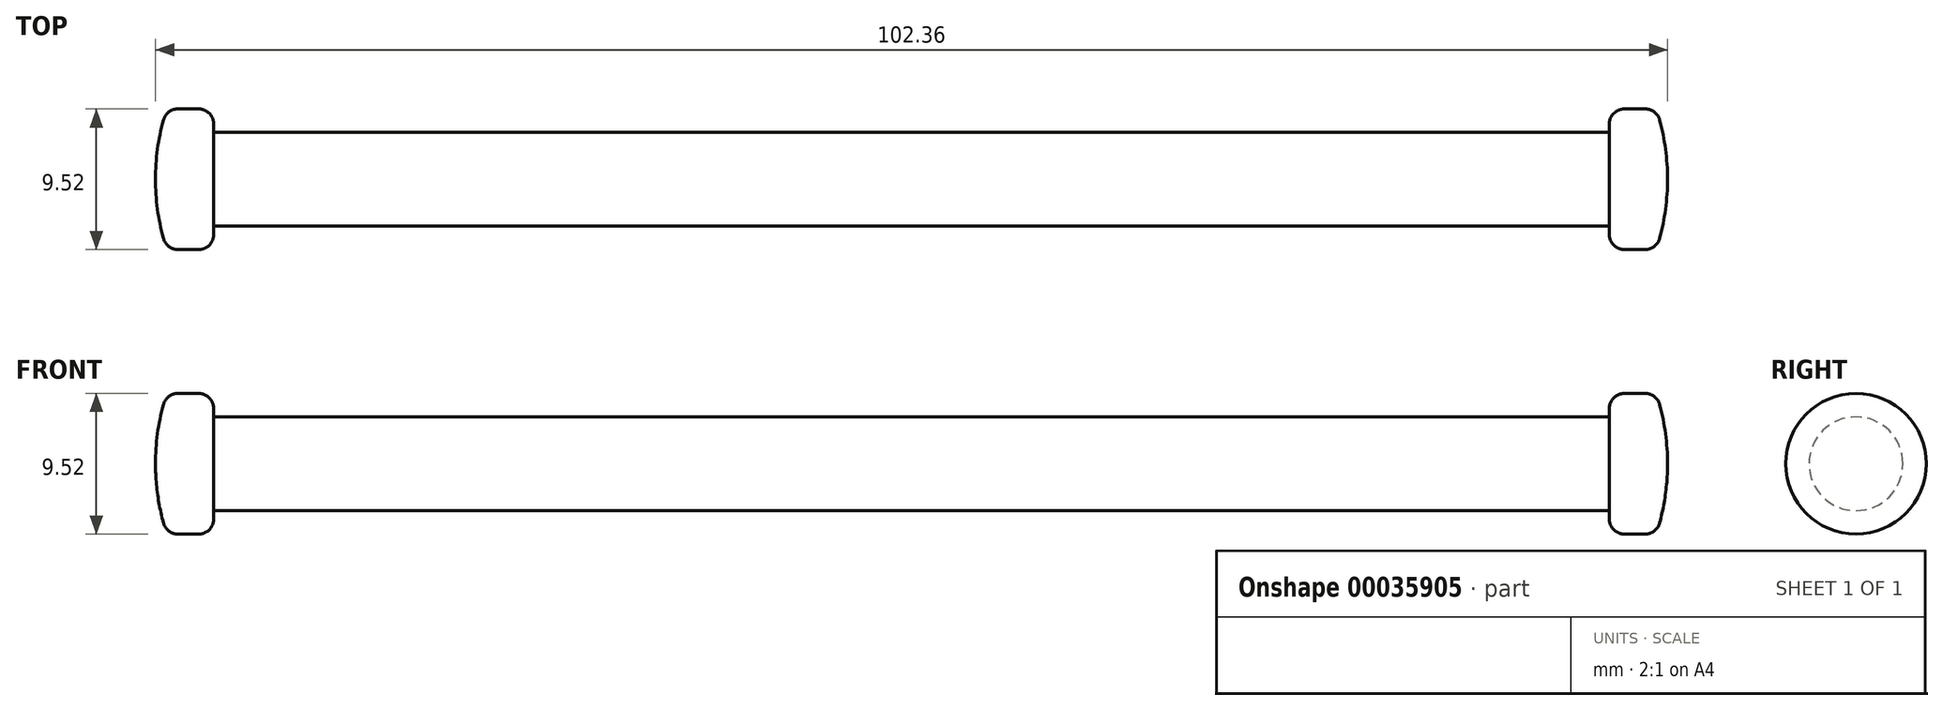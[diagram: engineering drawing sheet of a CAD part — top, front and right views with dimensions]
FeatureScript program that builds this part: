
annotation { "Feature Type Name" : "Feature", "Feature Type Description" : "" }
export const myFeature = defineFeature(function(context is Context, id is Id, definition is map)
    precondition{}
    {
        {
            var Q0;
            Q0=qCreatedBy(makeId("Front.planeOp"),FACE);
            var sketch = newSketch(context, id + "F0", { "sketchPlane" : qUnion([Q0])});
            skLineSegment(sketch, "E0", {"start": v(0, 24.03) * mm, "end": v(0, -23.14) * mm, "construction": true});
            skLineSegment(sketch, "E1", {"start": v(0, 0) * mm, "end": v(51.18, 0) * mm});
            skLineSegment(sketch, "E2", {"start": v(0, 0) * mm, "end": v(0, 3.18) * mm});
            skLineSegment(sketch, "E3", {"start": v(0, 3.18) * mm, "end": v(47.24, 3.18) * mm});
            skLineSegment(sketch, "E4", {"start": v(47.24, 3.18) * mm, "end": v(47.24, 3.75) * mm});
            skLineSegment(sketch, "E5", {"start": v(48.26, 4.76) * mm, "end": v(49.66, 4.76) * mm});
            skArc(sketch, "E6", {"start": v(51.18, 0) * mm, "mid": v(51.05, 2.02) * mm, "end": v(50.64, 4.01) * mm});
            skPoint(sketch, "E7.visualSharp", {"position": v(47.24, 4.76) * mm});
            skArc(sketch, "E7.filletArc", {"start": v(48.26, 4.76) * mm, "mid": v(47.54, 4.46) * mm, "end": v(47.24, 3.75) * mm});
            skPoint(sketch, "E8.visualSharp", {"position": v(50.42, 4.76) * mm});
            skArc(sketch, "E8.filletArc", {"start": v(50.64, 4.01) * mm, "mid": v(50.28, 4.55) * mm, "end": v(49.66, 4.76) * mm});
            skLineSegment(sketch, "E9", {"start": v(51.18, 0) * mm, "end": v(51.18, -2.62) * mm, "construction": true});
            skSolve(sketch);
        }
        {
            var Q0;
            Q0=makeQuery(id+"F0.imprint","IMPRINT",FACE,{"disambiguationData":[TD([[makeQuery(id+"F0.imprint","IMPRINT",EDGE,{"derivedFrom":sQuery(id+"F0.wireOp",EDGE,"E1")}),1.0]])]});
            var Q1;
            Q1=sQuery(id+"F0.wireOp",EDGE,"E1");
            revolve(context, id + "F1", {"entities" : qUnion([Q0]), "axis" : qUnion([Q1]), "revolveType" : RevolveType.FULL});
        }
        {
            var Q0;
            Q0=makeQuery(id+"F1.opRevolve","SWEPT_BODY",BODY,{"disambiguationData":[OSD([sQuery(id+"F0.wireOp",EDGE,"E1"),sQuery(id+"F0.wireOp",EDGE,"E2"),sQuery(id+"F0.wireOp",EDGE,"E3"),sQuery(id+"F0.wireOp",EDGE,"E4"),sQuery(id+"F0.wireOp",EDGE,"E5"),sQuery(id+"F0.wireOp",EDGE,"E6"),sQuery(id+"F0.wireOp",EDGE,"E7.filletArc"),sQuery(id+"F0.wireOp",EDGE,"E8.filletArc")])]});
            var Q1;
            Q1=qCreatedBy(makeId("Right.planeOp"),FACE);
            mirror(context, id + "F2", {"operationType" : NewBodyOperationType.ADD, "entities" : qUnion([Q0]), "mirrorPlane" : qUnion([Q1])});
        }
    });
